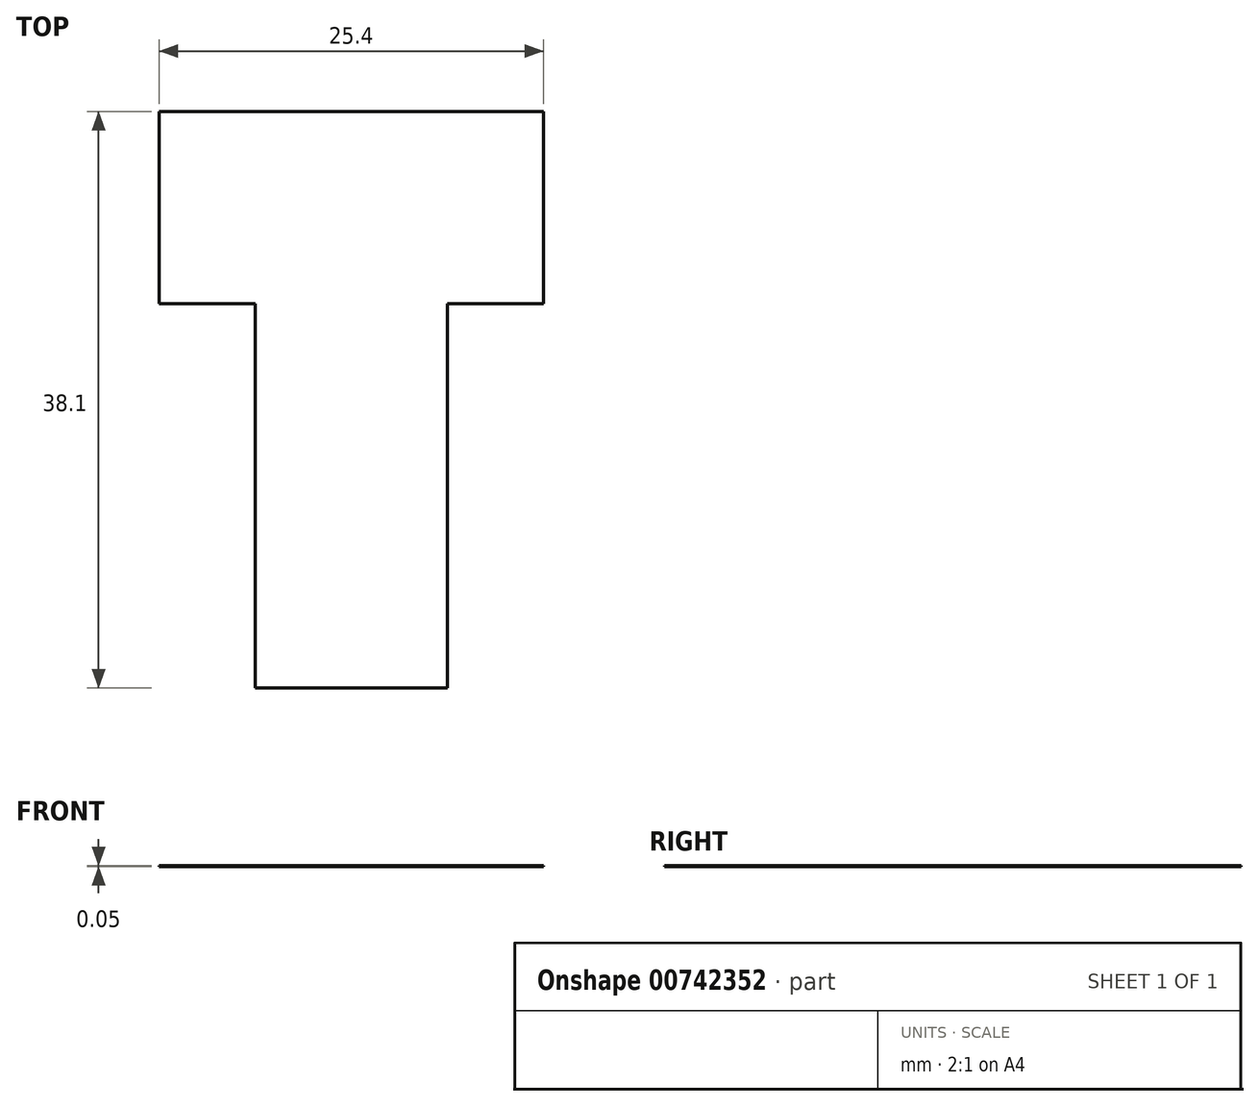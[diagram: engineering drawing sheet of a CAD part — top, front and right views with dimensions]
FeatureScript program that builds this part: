
annotation { "Feature Type Name" : "Feature", "Feature Type Description" : "" }
export const myFeature = defineFeature(function(context is Context, id is Id, definition is map)
    precondition{}
    {
        {
            var Q0;
            Q0=qCreatedBy(makeId("Top.planeOp"),FACE);
            var sketch = newSketch(context, id + "F0", { "sketchPlane" : qUnion([Q0])});
            skLineSegment(sketch, "E0", {"start": v(-6.35, 0) * mm, "end": v(-6.35, 25.4) * mm});
            skLineSegment(sketch, "E1", {"start": v(-6.35, 25.4) * mm, "end": v(-12.7, 25.4) * mm});
            skLineSegment(sketch, "E2", {"start": v(-12.7, 25.4) * mm, "end": v(-12.7, 38.1) * mm});
            skLineSegment(sketch, "E3", {"start": v(-12.7, 38.1) * mm, "end": v(0, 38.1) * mm});
            skLineSegment(sketch, "E4", {"start": v(0, 38.1) * mm, "end": v(12.7, 38.1) * mm});
            skLineSegment(sketch, "E5", {"start": v(12.7, 38.1) * mm, "end": v(12.7, 25.4) * mm});
            skLineSegment(sketch, "E6", {"start": v(12.7, 25.4) * mm, "end": v(6.35, 25.4) * mm});
            skLineSegment(sketch, "E7", {"start": v(6.35, 25.4) * mm, "end": v(6.35, 0) * mm});
            skLineSegment(sketch, "E8", {"start": v(6.35, 0) * mm, "end": v(-6.35, 0) * mm});
            skSolve(sketch);
        }
        {
            var Q0;
            Q0 = qSketchRegion(id + "F0", true);
            extrude(context, id + "F1", {"entities" : qUnion([Q0]), "depth" : 5 / 101.6 * mm, "offsetDistance" : 25.4 * mm});
        }
    });
